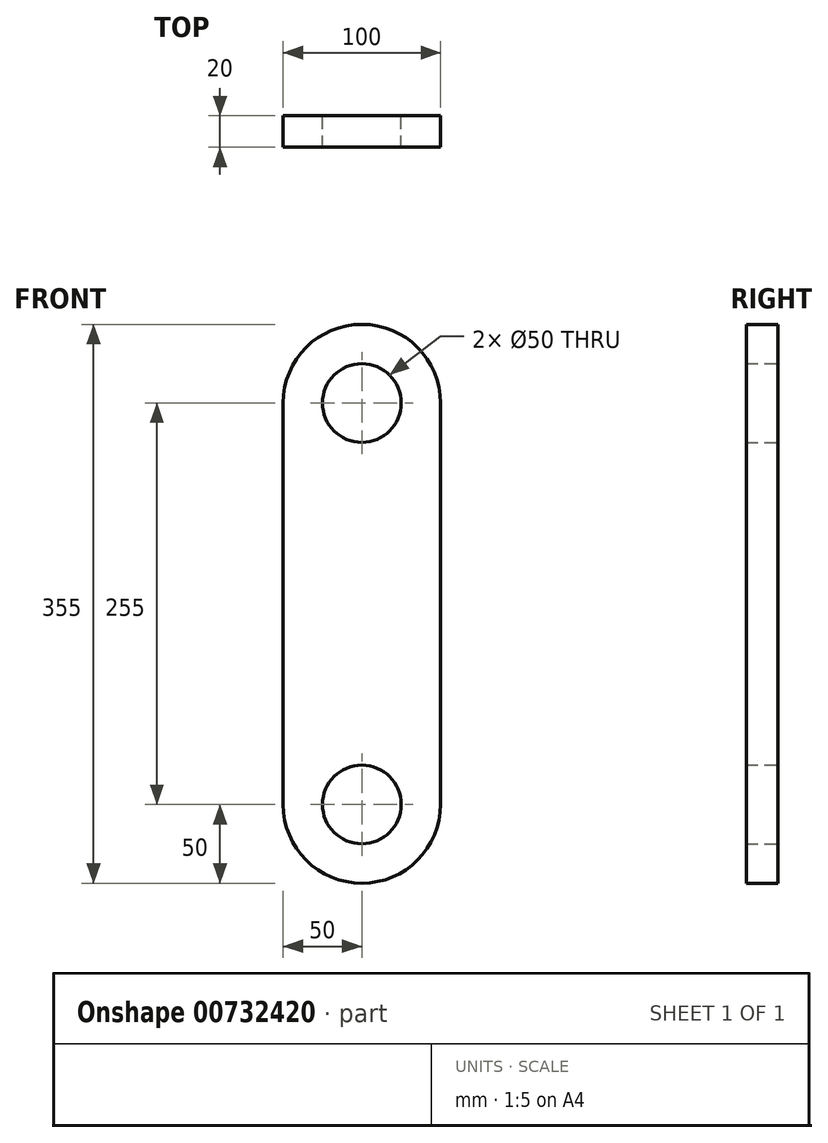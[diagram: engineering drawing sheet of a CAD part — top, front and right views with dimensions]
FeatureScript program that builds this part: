
annotation { "Feature Type Name" : "Feature", "Feature Type Description" : "" }
export const myFeature = defineFeature(function(context is Context, id is Id, definition is map)
    precondition{}
    {
        {
            var Q0;
            Q0=qCreatedBy(makeId("Front.planeOp"),FACE);
            var sketch = newSketch(context, id + "F0", { "sketchPlane" : qUnion([Q0])});
            skLineSegment(sketch, "E0.bottom", {"start": v(50, -177.5) * mm, "end": v(-50, -177.5) * mm});
            skLineSegment(sketch, "E0.top", {"start": v(50, 177.5) * mm, "end": v(-50, 177.5) * mm});
            skLineSegment(sketch, "E0.left", {"start": v(50, -177.5) * mm, "end": v(50, 177.5) * mm});
            skLineSegment(sketch, "E0.right", {"start": v(-50, -177.5) * mm, "end": v(-50, 177.5) * mm});
            skPoint(sketch, "E0.middle", {"position": v(0, 0) * mm});
            skCircle(sketch, "E1", {"center": v(0, 127.5) * mm, "radius": 25 * mm});
            skCircle(sketch, "E2", {"center": v(0, -127.5) * mm, "radius": 25 * mm});
            skSolve(sketch);
        }
        {
            var Q0;
            Q0 = qSketchRegion(id + "F0", true);
            extrude(context, id + "F1", {"entities" : qUnion([Q0]), "depth" : 20 * mm, "offsetDistance" : 25 * mm});
        }
        {
            var Q0;
            Q0=makeQuery(id+"F1.opExtrude","SWEPT_EDGE",EDGE,{"disambiguationData":[OSD([sQuery(id+"F0.wireOp",EDGE,"E0.top"),sQuery(id+"F0.wireOp",EDGE,"E0.left")])]});
            var Q1;
            Q1=makeQuery(id+"F1.opExtrude","SWEPT_EDGE",EDGE,{"disambiguationData":[OSD([sQuery(id+"F0.wireOp",EDGE,"E0.top"),sQuery(id+"F0.wireOp",EDGE,"E0.right")])]});
            var Q2;
            Q2=makeQuery(id+"F1.opExtrude","SWEPT_EDGE",EDGE,{"disambiguationData":[OSD([sQuery(id+"F0.wireOp",EDGE,"E0.bottom"),sQuery(id+"F0.wireOp",EDGE,"E0.left")])]});
            var Q3;
            Q3=makeQuery(id+"F1.opExtrude","SWEPT_EDGE",EDGE,{"disambiguationData":[OSD([sQuery(id+"F0.wireOp",EDGE,"E0.bottom"),sQuery(id+"F0.wireOp",EDGE,"E0.right")])]});
            fillet(context, id + "F2", {"entities" : qUnion([Q0, Q1, Q2, Q3]), "radius" : 50 * mm, "tangentPropagation" : true, "allowEdgeOverflow" : false});
        }
    });
